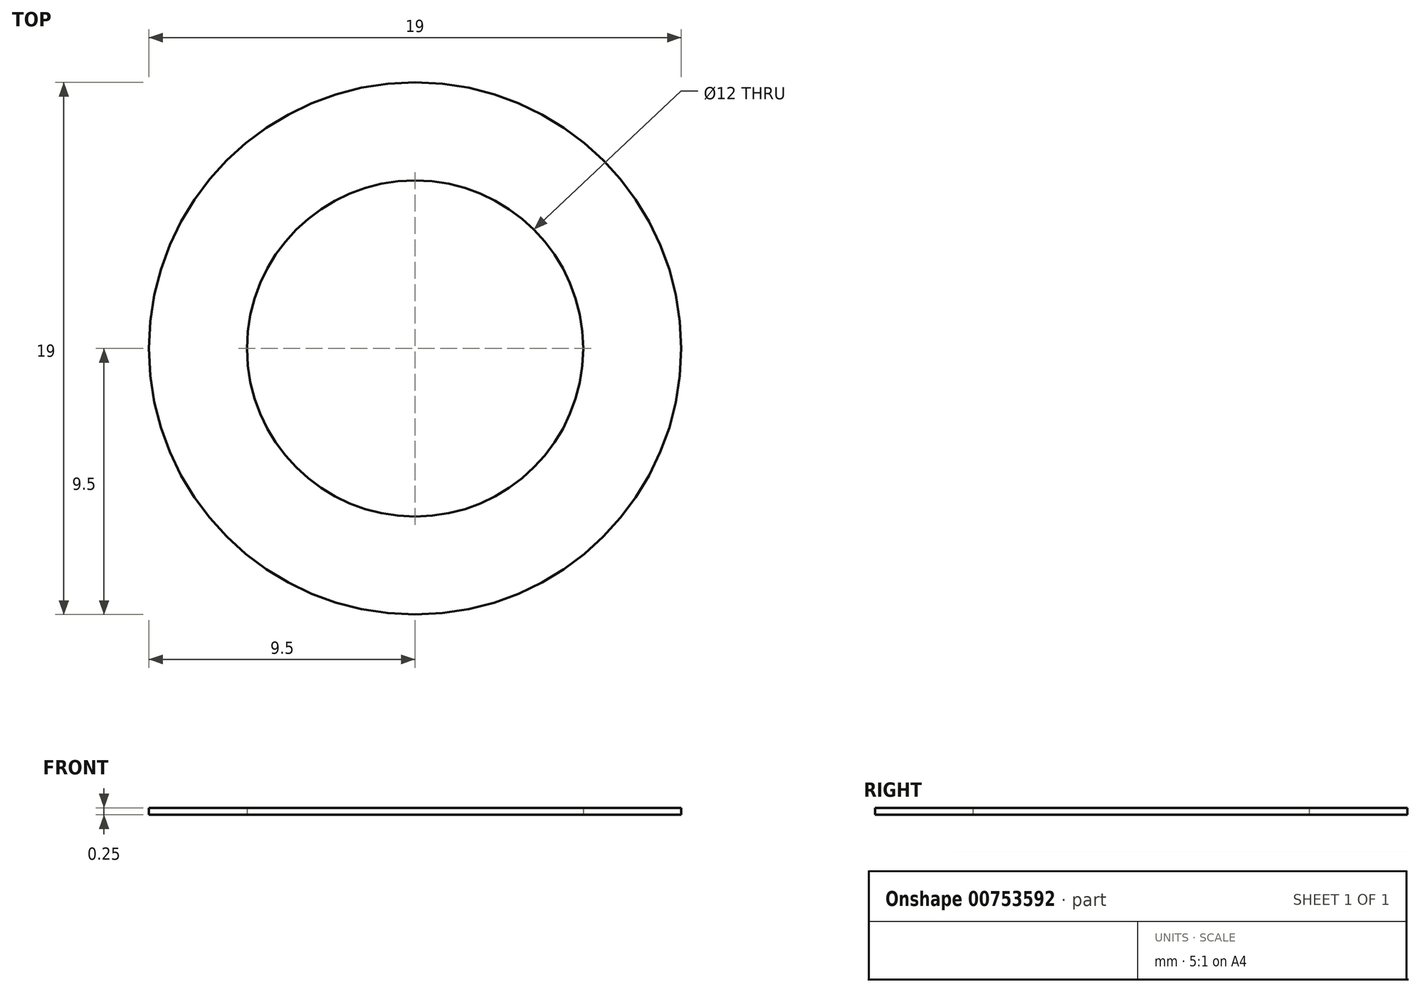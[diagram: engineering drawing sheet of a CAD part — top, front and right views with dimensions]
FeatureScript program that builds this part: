
annotation { "Feature Type Name" : "Feature", "Feature Type Description" : "" }
export const myFeature = defineFeature(function(context is Context, id is Id, definition is map)
    precondition{}
    {
        {
            var Q0;
            Q0=qCreatedBy(makeId("Top.planeOp"),FACE);
            var sketch = newSketch(context, id + "F0", { "sketchPlane" : qUnion([Q0])});
            skLineSegment(sketch, "E0", {"start": v(0, 0) * mm, "end": v(4, 0) * mm});
            skLineSegment(sketch, "E1", {"start": v(4, 0) * mm, "end": v(11, 0) * mm});
            skLineSegment(sketch, "E2", {"start": v(11, 0) * mm, "end": v(11, -2.01) * mm});
            skLineSegment(sketch, "E3", {"start": v(11, -2.01) * mm, "end": v(10, -2.01) * mm});
            skLineSegment(sketch, "E4", {"start": v(10, -2.01) * mm, "end": v(9.5, -2.01) * mm});
            skLineSegment(sketch, "E5", {"start": v(9.5, -2.01) * mm, "end": v(9.5, 0) * mm});
            skLineSegment(sketch, "E6", {"start": v(4, 0) * mm, "end": v(4, -2.37) * mm});
            skLineSegment(sketch, "E7", {"start": v(4, -2.37) * mm, "end": v(6, -2.37) * mm});
            skLineSegment(sketch, "E8", {"start": v(6, -2.37) * mm, "end": v(6, 0) * mm});
            skCircle(sketch, "E9", {"center": v(0, 0) * mm, "radius": 6 * mm});
            skCircle(sketch, "E10", {"center": v(0, 0) * mm, "radius": 9.5 * mm});
            skSolve(sketch);
        }
        {
            var Q0;
            {var subQ0=sQuery(id+"F0.wireOp",EDGE,"E8");Q0=makeQuery(id+"F0.imprint","IMPRINT",FACE,{"disambiguationData":[TD([[makeQuery(id+"F0.imprint","IMPRINT",EDGE,{"derivedFrom":subQ0}),-1.0]])]});}
            var Q1;
            {var subQ0=sQuery(id+"F0.wireOp",EDGE,"E8");Q1=makeQuery(id+"F0.imprint","IMPRINT",FACE,{"disambiguationData":[TD([[makeQuery(id+"F0.imprint","IMPRINT",EDGE,{"derivedFrom":subQ0}),1.0]])]});}
            extrude(context, id + "F1", {"entities" : qUnion([Q0, Q1]), "depth" : 0.25 * mm, "offsetDistance" : 25 * mm});
        }
    });
